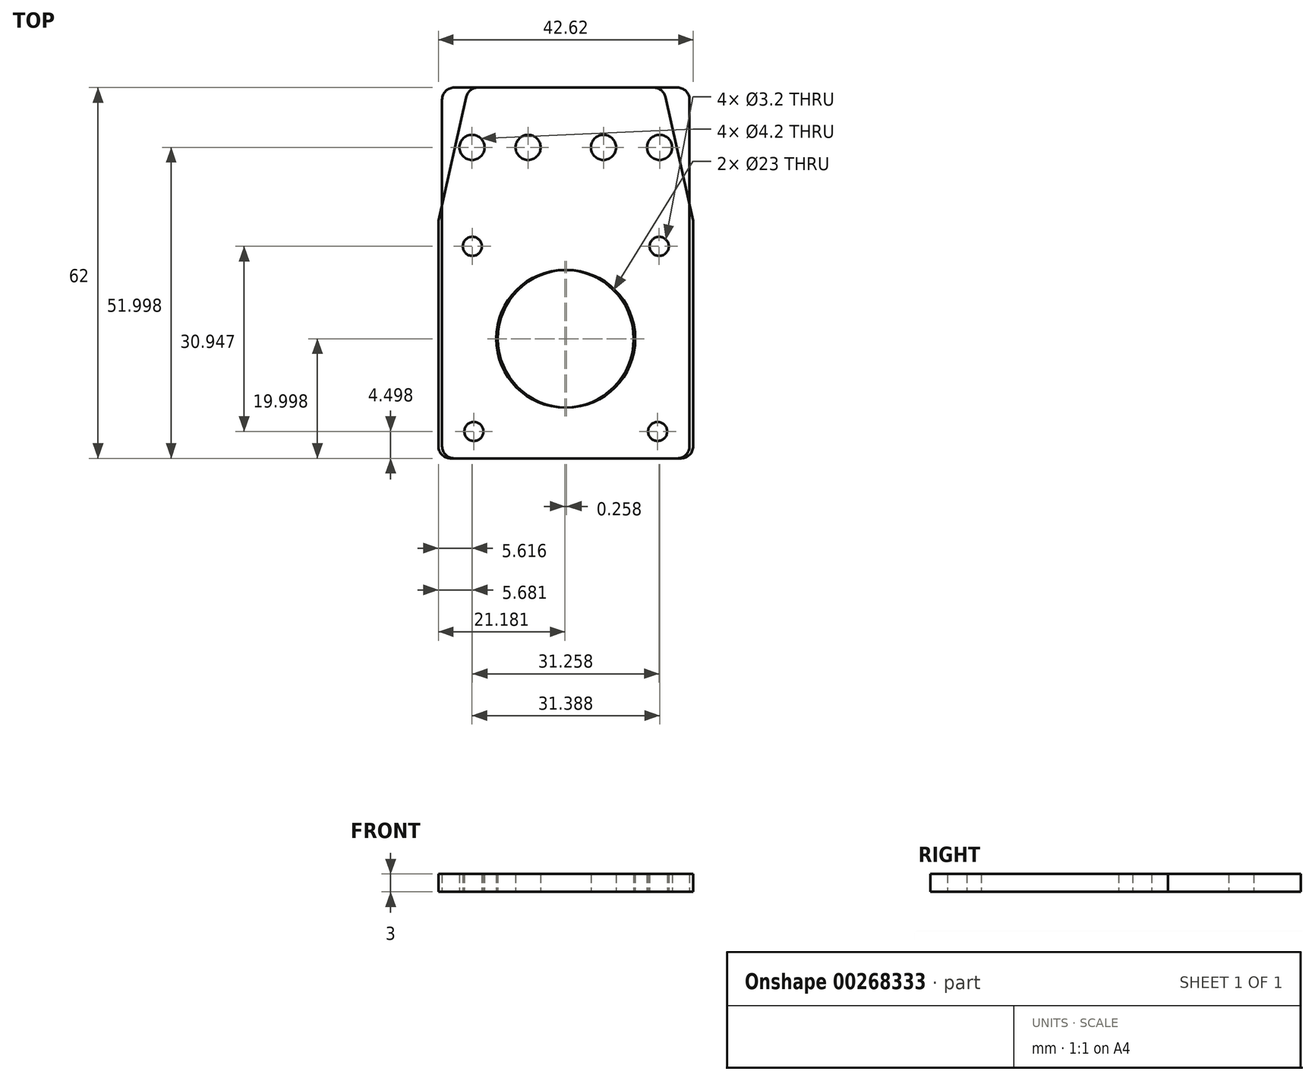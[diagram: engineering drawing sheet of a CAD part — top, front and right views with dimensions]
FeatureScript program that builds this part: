
annotation { "Feature Type Name" : "Feature", "Feature Type Description" : "" }
export const myFeature = defineFeature(function(context is Context, id is Id, definition is map)
    precondition{}
    {
        {
            var Q0;
            Q0=qCreatedBy(makeId("Top.planeOp"),FACE);
            var sketch = newSketch(context, id + "F0", { "sketchPlane" : qUnion([Q0])});
            skCircle(sketch, "E0", {"center": v(-0.13, -28.42) * mm, "radius": 11.5 * mm});
            skCircle(sketch, "E1", {"center": v(15.37, -43.92) * mm, "radius": 1.6 * mm});
            skCircle(sketch, "E2", {"center": v(-15.63, -12.97) * mm, "radius": 1.6 * mm});
            skLineSegment(sketch, "E3.bottom", {"start": v(-18.7, 13.58) * mm, "end": v(14.7, 13.58) * mm});
            skLineSegment(sketch, "E3.top", {"start": v(-18.7, -48.42) * mm, "end": v(19.3, -48.42) * mm});
            skLineSegment(sketch, "E3.left", {"start": v(-20.7, 11.58) * mm, "end": v(-20.7, -46.42) * mm});
            skLineSegment(sketch, "E3.right", {"start": v(21.3, -8.68) * mm, "end": v(21.3, -46.42) * mm});
            skCircle(sketch, "E4", {"center": v(-15.7, 3.58) * mm, "radius": 2.1 * mm});
            skCircle(sketch, "E5", {"center": v(6.3, 3.58) * mm, "radius": 2.1 * mm});
            skPoint(sketch, "E6.visualSharp", {"position": v(-20.7, 13.58) * mm});
            skArc(sketch, "E6.filletArc", {"start": v(-18.7, 13.58) * mm, "mid": v(-20.1, 13) * mm, "end": v(-20.7, 11.58) * mm});
            skPoint(sketch, "E7.visualSharp", {"position": v(21.3, -48.42) * mm});
            skArc(sketch, "E7.filletArc", {"start": v(19.3, -48.42) * mm, "mid": v(20.72, -47.84) * mm, "end": v(21.3, -46.42) * mm});
            skPoint(sketch, "E8.visualSharp", {"position": v(-20.7, -48.42) * mm});
            skArc(sketch, "E8.filletArc", {"start": v(-20.7, -46.42) * mm, "mid": v(-20.1, -47.84) * mm, "end": v(-18.7, -48.42) * mm});
            skLineSegment(sketch, "E9", {"start": v(16.66, 12.02) * mm, "end": v(21.3, -8.68) * mm});
            skPoint(sketch, "E10.visualSharp", {"position": v(16.3, 13.58) * mm});
            skArc(sketch, "E10.filletArc", {"start": v(16.66, 12.02) * mm, "mid": v(15.96, 13.14) * mm, "end": v(14.7, 13.58) * mm});
            skSolve(sketch);
        }
        {
            var Q0;
            Q0=qSketchRegion(id+"F0",true);
            extrude(context, id + "F1", {"entities" : qUnion([Q0]), "depth" : 3 * mm});
        }
        {
            var Q0;
            Q0=makeQuery(id+"F1.opExtrude","SWEPT_BODY",BODY,{"disambiguationData":[OSD([sQuery(id+"F0.wireOp",EDGE,"E0"),sQuery(id+"F0.wireOp",EDGE,"E1"),sQuery(id+"F0.wireOp",EDGE,"E2"),sQuery(id+"F0.wireOp",EDGE,"E3.bottom"),sQuery(id+"F0.wireOp",EDGE,"E3.top"),sQuery(id+"F0.wireOp",EDGE,"E3.left"),sQuery(id+"F0.wireOp",EDGE,"E3.right"),sQuery(id+"F0.wireOp",EDGE,"E4"),sQuery(id+"F0.wireOp",EDGE,"E5"),sQuery(id+"F0.wireOp",EDGE,"E6.filletArc"),sQuery(id+"F0.wireOp",EDGE,"E7.filletArc"),sQuery(id+"F0.wireOp",EDGE,"E8.filletArc"),sQuery(id+"F0.wireOp",EDGE,"E9")])]});
            var Q1;
            Q1=qCreatedBy(makeId("Right.planeOp"),FACE);
            mirror(context, id + "F2", {"entities" : qUnion([Q0]), "mirrorPlane" : qUnion([Q1])});
        }
    });
